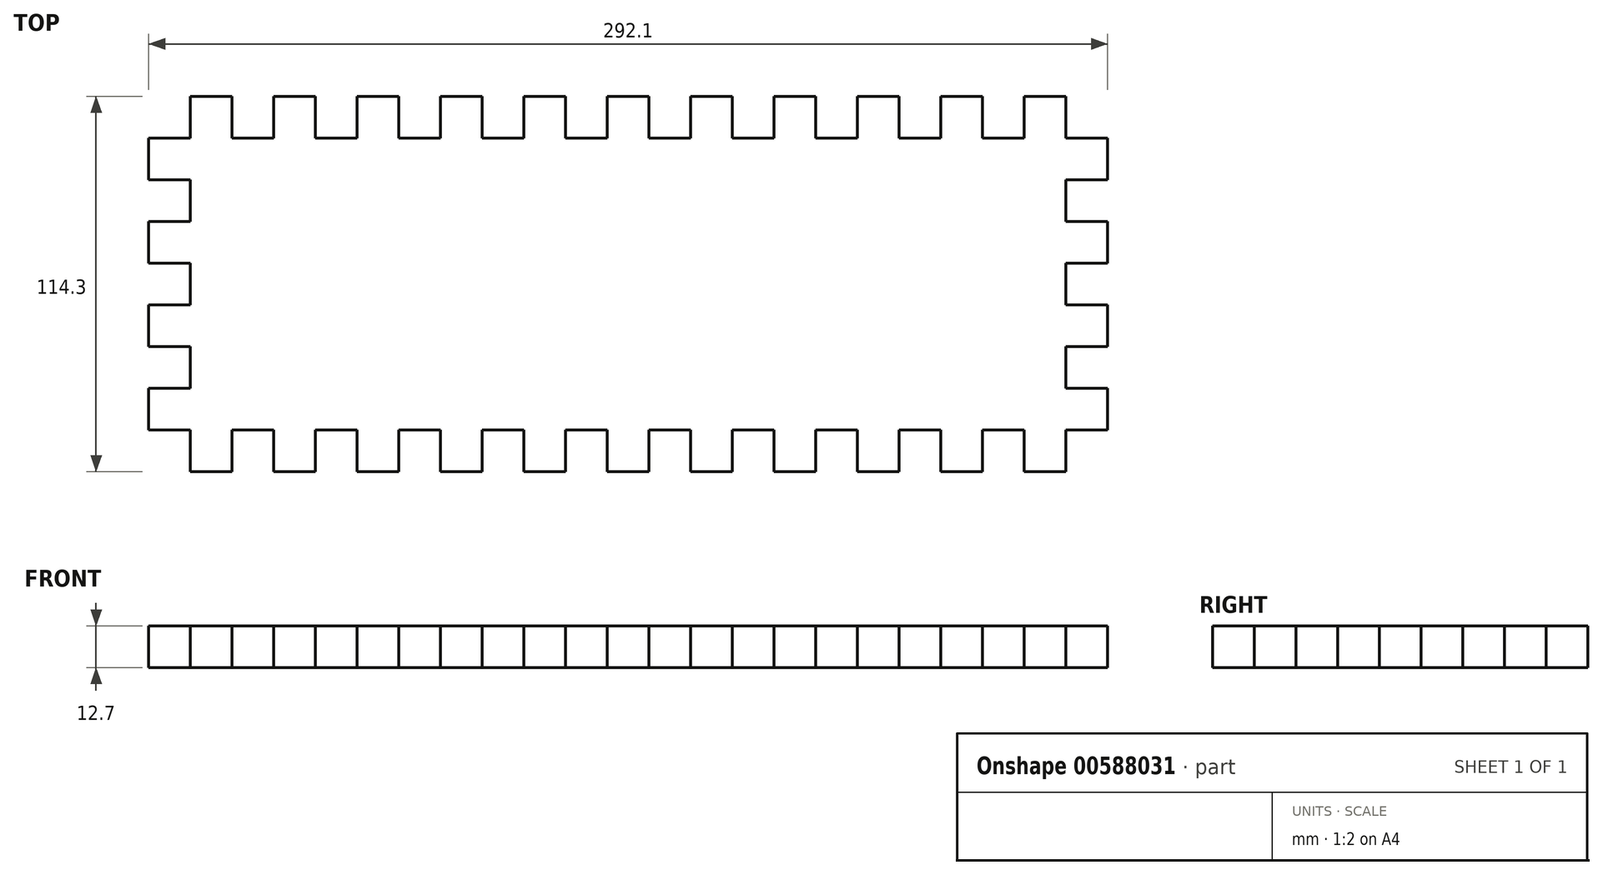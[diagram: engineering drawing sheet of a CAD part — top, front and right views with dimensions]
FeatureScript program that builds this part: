
annotation { "Feature Type Name" : "Feature", "Feature Type Description" : "" }
export const myFeature = defineFeature(function(context is Context, id is Id, definition is map)
    precondition{}
    {
        {
            var Q0;
            Q0=qCreatedBy(makeId("Top.planeOp"),FACE);
            var sketch = newSketch(context, id + "F0", { "sketchPlane" : qUnion([Q0])});
            skLineSegment(sketch, "E0.top", {"start": v(12.7, 114.3) * mm, "end": v(25.4, 114.3) * mm});
            skLineSegment(sketch, "E0.right", {"start": v(292.1, 12.7) * mm, "end": v(292.1, 25.4) * mm});
            skLineSegment(sketch, "E1", {"start": v(25.4, 101.6) * mm, "end": v(38.1, 101.6) * mm});
            skLineSegment(sketch, "E2", {"start": v(279.4, 88.9) * mm, "end": v(279.4, 76.2) * mm});
            skLineSegment(sketch, "E3", {"start": v(12.7, 101.6) * mm, "end": v(12.7, 114.3) * mm});
            skLineSegment(sketch, "E4", {"start": v(12.7, 101.6) * mm, "end": v(0, 101.6) * mm});
            skLineSegment(sketch, "E5.1.0.0", {"start": v(25.4, 101.6) * mm, "end": v(25.4, 114.3) * mm});
            skLineSegment(sketch, "E5.2.0.0", {"start": v(38.1, 101.6) * mm, "end": v(38.1, 114.3) * mm});
            skLineSegment(sketch, "E5.3.0.0", {"start": v(50.8, 101.6) * mm, "end": v(50.8, 114.3) * mm});
            skLineSegment(sketch, "E5.4.0.0", {"start": v(63.5, 101.6) * mm, "end": v(63.5, 114.3) * mm});
            skLineSegment(sketch, "E5.5.0.0", {"start": v(76.2, 101.6) * mm, "end": v(76.2, 114.3) * mm});
            skLineSegment(sketch, "E5.6.0.0", {"start": v(88.9, 101.6) * mm, "end": v(88.9, 114.3) * mm});
            skLineSegment(sketch, "E5.7.0.0", {"start": v(101.6, 101.6) * mm, "end": v(101.6, 114.3) * mm});
            skLineSegment(sketch, "E5.8.0.0", {"start": v(114.3, 101.6) * mm, "end": v(114.3, 114.3) * mm});
            skLineSegment(sketch, "E5.9.0.0", {"start": v(127, 101.6) * mm, "end": v(127, 114.3) * mm});
            skLineSegment(sketch, "E5.10.0.0", {"start": v(139.7, 101.6) * mm, "end": v(139.7, 114.3) * mm});
            skLineSegment(sketch, "E5.11.0.0", {"start": v(152.4, 101.6) * mm, "end": v(152.4, 114.3) * mm});
            skLineSegment(sketch, "E5.12.0.0", {"start": v(165.1, 101.6) * mm, "end": v(165.1, 114.3) * mm});
            skLineSegment(sketch, "E5.13.0.0", {"start": v(177.8, 101.6) * mm, "end": v(177.8, 114.3) * mm});
            skLineSegment(sketch, "E5.14.0.0", {"start": v(190.5, 101.6) * mm, "end": v(190.5, 114.3) * mm});
            skLineSegment(sketch, "E5.15.0.0", {"start": v(203.2, 101.6) * mm, "end": v(203.2, 114.3) * mm});
            skLineSegment(sketch, "E5.16.0.0", {"start": v(215.9, 101.6) * mm, "end": v(215.9, 114.3) * mm});
            skLineSegment(sketch, "E5.17.0.0", {"start": v(228.6, 101.6) * mm, "end": v(228.6, 114.3) * mm});
            skLineSegment(sketch, "E5.18.0.0", {"start": v(241.3, 101.6) * mm, "end": v(241.3, 114.3) * mm});
            skLineSegment(sketch, "E5.19.0.0", {"start": v(254, 101.6) * mm, "end": v(254, 114.3) * mm});
            skLineSegment(sketch, "E5.20.0.0", {"start": v(266.7, 101.6) * mm, "end": v(266.7, 114.3) * mm});
            skLineSegment(sketch, "E5.21.0.0", {"start": v(279.4, 101.6) * mm, "end": v(279.4, 114.3) * mm});
            skLineSegment(sketch, "E6.trimOffspring", {"start": v(38.1, 114.3) * mm, "end": v(50.8, 114.3) * mm});
            skLineSegment(sketch, "E7.trimOffspring", {"start": v(63.5, 114.3) * mm, "end": v(76.2, 114.3) * mm});
            skLineSegment(sketch, "E8.trimOffspring", {"start": v(88.9, 114.3) * mm, "end": v(101.6, 114.3) * mm});
            skLineSegment(sketch, "E9.trimOffspring", {"start": v(114.3, 114.3) * mm, "end": v(127, 114.3) * mm});
            skLineSegment(sketch, "E10.trimOffspring", {"start": v(139.7, 114.3) * mm, "end": v(152.4, 114.3) * mm});
            skLineSegment(sketch, "E11.trimOffspring", {"start": v(165.1, 114.3) * mm, "end": v(177.8, 114.3) * mm});
            skLineSegment(sketch, "E12.trimOffspring", {"start": v(190.5, 114.3) * mm, "end": v(203.2, 114.3) * mm});
            skLineSegment(sketch, "E13.trimOffspring", {"start": v(215.9, 114.3) * mm, "end": v(228.6, 114.3) * mm});
            skLineSegment(sketch, "E14.trimOffspring", {"start": v(241.3, 114.3) * mm, "end": v(254, 114.3) * mm});
            skLineSegment(sketch, "E15.trimOffspring", {"start": v(266.7, 114.3) * mm, "end": v(279.4, 114.3) * mm});
            skLineSegment(sketch, "E16.trimOffspring", {"start": v(254, 101.6) * mm, "end": v(266.7, 101.6) * mm});
            skLineSegment(sketch, "E17.trimOffspring", {"start": v(228.6, 101.6) * mm, "end": v(241.3, 101.6) * mm});
            skLineSegment(sketch, "E18.trimOffspring", {"start": v(203.2, 101.6) * mm, "end": v(215.9, 101.6) * mm});
            skLineSegment(sketch, "E19.trimOffspring", {"start": v(177.8, 101.6) * mm, "end": v(190.5, 101.6) * mm});
            skLineSegment(sketch, "E20.trimOffspring", {"start": v(152.4, 101.6) * mm, "end": v(165.1, 101.6) * mm});
            skLineSegment(sketch, "E21.trimOffspring", {"start": v(127, 101.6) * mm, "end": v(139.7, 101.6) * mm});
            skLineSegment(sketch, "E22.trimOffspring", {"start": v(101.6, 101.6) * mm, "end": v(114.3, 101.6) * mm});
            skLineSegment(sketch, "E23.trimOffspring", {"start": v(76.2, 101.6) * mm, "end": v(88.9, 101.6) * mm});
            skLineSegment(sketch, "E24.trimOffspring", {"start": v(50.8, 101.6) * mm, "end": v(63.5, 101.6) * mm});
            skLineSegment(sketch, "E25", {"start": v(279.4, 101.6) * mm, "end": v(292.1, 101.6) * mm});
            skLineSegment(sketch, "E26.0.1.0", {"start": v(279.4, 88.9) * mm, "end": v(292.1, 88.9) * mm});
            skLineSegment(sketch, "E26.0.2.0", {"start": v(279.4, 76.2) * mm, "end": v(292.1, 76.2) * mm});
            skLineSegment(sketch, "E26.0.3.0", {"start": v(279.4, 63.5) * mm, "end": v(292.1, 63.5) * mm});
            skLineSegment(sketch, "E26.0.4.0", {"start": v(279.4, 50.8) * mm, "end": v(292.1, 50.8) * mm});
            skLineSegment(sketch, "E26.0.5.0", {"start": v(279.4, 38.1) * mm, "end": v(292.1, 38.1) * mm});
            skLineSegment(sketch, "E26.0.6.0", {"start": v(279.4, 25.4) * mm, "end": v(292.1, 25.4) * mm});
            skLineSegment(sketch, "E26.0.7.0", {"start": v(279.4, 12.7) * mm, "end": v(292.1, 12.7) * mm});
            skLineSegment(sketch, "E27.trimOffspring", {"start": v(279.4, 63.5) * mm, "end": v(279.4, 50.8) * mm});
            skLineSegment(sketch, "E28.trimOffspring", {"start": v(279.4, 38.1) * mm, "end": v(279.4, 25.4) * mm});
            skLineSegment(sketch, "E29.trimOffspring", {"start": v(292.1, 38.1) * mm, "end": v(292.1, 50.8) * mm});
            skLineSegment(sketch, "E30.trimOffspring", {"start": v(292.1, 63.5) * mm, "end": v(292.1, 76.2) * mm});
            skLineSegment(sketch, "E31.trimOffspring", {"start": v(292.1, 88.9) * mm, "end": v(292.1, 101.6) * mm});
            skLineSegment(sketch, "E32", {"start": v(279.4, 12.7) * mm, "end": v(279.4, 0) * mm});
            skLineSegment(sketch, "E33.MirrorCS", {"start": v(0, 63.5) * mm, "end": v(0, 76.2) * mm});
            skLineSegment(sketch, "E34.MirrorCS", {"start": v(12.7, 38.1) * mm, "end": v(12.7, 25.4) * mm});
            skLineSegment(sketch, "E35.MirrorCS", {"start": v(12.7, 12.7) * mm, "end": v(0, 12.7) * mm});
            skLineSegment(sketch, "E36.MirrorCS", {"start": v(12.7, 76.2) * mm, "end": v(0, 76.2) * mm});
            skLineSegment(sketch, "E37.MirrorCS", {"start": v(12.7, 25.4) * mm, "end": v(0, 25.4) * mm});
            skLineSegment(sketch, "E38.MirrorCS", {"start": v(12.7, 38.1) * mm, "end": v(0, 38.1) * mm});
            skLineSegment(sketch, "E39.MirrorCS", {"start": v(12.7, 88.9) * mm, "end": v(0, 88.9) * mm});
            skLineSegment(sketch, "E40.MirrorCS", {"start": v(12.7, 12.7) * mm, "end": v(12.7, 0) * mm});
            skLineSegment(sketch, "E41.MirrorCS", {"start": v(12.7, 50.8) * mm, "end": v(0, 50.8) * mm});
            skLineSegment(sketch, "E42.MirrorCS", {"start": v(12.7, 63.5) * mm, "end": v(12.7, 50.8) * mm});
            skLineSegment(sketch, "E43.MirrorCS", {"start": v(0, 38.1) * mm, "end": v(0, 50.8) * mm});
            skLineSegment(sketch, "E44.MirrorCS", {"start": v(0, 12.7) * mm, "end": v(0, 25.4) * mm});
            skLineSegment(sketch, "E45.MirrorCS", {"start": v(12.7, 88.9) * mm, "end": v(12.7, 76.2) * mm});
            skLineSegment(sketch, "E46.MirrorCS", {"start": v(0, 88.9) * mm, "end": v(0, 101.6) * mm});
            skLineSegment(sketch, "E47.MirrorCS", {"start": v(12.7, 63.5) * mm, "end": v(0, 63.5) * mm});
            skLineSegment(sketch, "E48.MirrorCS", {"start": v(139.7, 0) * mm, "end": v(152.4, 0) * mm});
            skLineSegment(sketch, "E49.MirrorCS", {"start": v(63.5, 0) * mm, "end": v(76.2, 0) * mm});
            skLineSegment(sketch, "E50.MirrorCS", {"start": v(76.2, 12.7) * mm, "end": v(88.9, 12.7) * mm});
            skLineSegment(sketch, "E51.MirrorCS", {"start": v(152.4, 12.7) * mm, "end": v(165.1, 12.7) * mm});
            skLineSegment(sketch, "E52.MirrorCS", {"start": v(266.7, 12.7) * mm, "end": v(266.7, 0) * mm});
            skLineSegment(sketch, "E53.MirrorCS", {"start": v(177.8, 12.7) * mm, "end": v(177.8, 0) * mm});
            skLineSegment(sketch, "E54.MirrorCS", {"start": v(215.9, 0) * mm, "end": v(228.6, 0) * mm});
            skLineSegment(sketch, "E55.MirrorCS", {"start": v(165.1, 0) * mm, "end": v(177.8, 0) * mm});
            skLineSegment(sketch, "E56.MirrorCS", {"start": v(241.3, 12.7) * mm, "end": v(241.3, 0) * mm});
            skLineSegment(sketch, "E57.MirrorCS", {"start": v(177.8, 12.7) * mm, "end": v(190.5, 12.7) * mm});
            skLineSegment(sketch, "E58.MirrorCS", {"start": v(152.4, 12.7) * mm, "end": v(152.4, 0) * mm});
            skLineSegment(sketch, "E59.MirrorCS", {"start": v(241.3, 0) * mm, "end": v(254, 0) * mm});
            skLineSegment(sketch, "E60.MirrorCS", {"start": v(38.1, 0) * mm, "end": v(50.8, 0) * mm});
            skLineSegment(sketch, "E61.MirrorCS", {"start": v(127, 12.7) * mm, "end": v(139.7, 12.7) * mm});
            skLineSegment(sketch, "E62.MirrorCS", {"start": v(254, 12.7) * mm, "end": v(254, 0) * mm});
            skLineSegment(sketch, "E63.MirrorCS", {"start": v(203.2, 12.7) * mm, "end": v(215.9, 12.7) * mm});
            skLineSegment(sketch, "E64.MirrorCS", {"start": v(165.1, 12.7) * mm, "end": v(165.1, 0) * mm});
            skLineSegment(sketch, "E65.MirrorCS", {"start": v(139.7, 12.7) * mm, "end": v(139.7, 0) * mm});
            skLineSegment(sketch, "E66.MirrorCS", {"start": v(228.6, 12.7) * mm, "end": v(228.6, 0) * mm});
            skLineSegment(sketch, "E67.MirrorCS", {"start": v(228.6, 12.7) * mm, "end": v(241.3, 12.7) * mm});
            skLineSegment(sketch, "E68.MirrorCS", {"start": v(25.4, 12.7) * mm, "end": v(38.1, 12.7) * mm});
            skLineSegment(sketch, "E69.MirrorCS", {"start": v(12.7, 0) * mm, "end": v(25.4, 0) * mm});
            skLineSegment(sketch, "E70.MirrorCS", {"start": v(114.3, 12.7) * mm, "end": v(114.3, 0) * mm});
            skLineSegment(sketch, "E71.MirrorCS", {"start": v(25.4, 12.7) * mm, "end": v(25.4, 0) * mm});
            skLineSegment(sketch, "E72.MirrorCS", {"start": v(38.1, 12.7) * mm, "end": v(38.1, 0) * mm});
            skLineSegment(sketch, "E73.MirrorCS", {"start": v(50.8, 12.7) * mm, "end": v(50.8, 0) * mm});
            skLineSegment(sketch, "E74.MirrorCS", {"start": v(127, 12.7) * mm, "end": v(127, 0) * mm});
            skLineSegment(sketch, "E75.MirrorCS", {"start": v(190.5, 0) * mm, "end": v(203.2, 0) * mm});
            skLineSegment(sketch, "E76.MirrorCS", {"start": v(190.5, 12.7) * mm, "end": v(190.5, 0) * mm});
            skLineSegment(sketch, "E77.MirrorCS", {"start": v(63.5, 12.7) * mm, "end": v(63.5, 0) * mm});
            skLineSegment(sketch, "E78.MirrorCS", {"start": v(76.2, 12.7) * mm, "end": v(76.2, 0) * mm});
            skLineSegment(sketch, "E79.MirrorCS", {"start": v(114.3, 0) * mm, "end": v(127, 0) * mm});
            skLineSegment(sketch, "E80.MirrorCS", {"start": v(215.9, 12.7) * mm, "end": v(215.9, 0) * mm});
            skLineSegment(sketch, "E81.MirrorCS", {"start": v(203.2, 12.7) * mm, "end": v(203.2, 0) * mm});
            skLineSegment(sketch, "E82.MirrorCS", {"start": v(101.6, 12.7) * mm, "end": v(114.3, 12.7) * mm});
            skLineSegment(sketch, "E83.MirrorCS", {"start": v(266.7, 0) * mm, "end": v(279.4, 0) * mm});
            skLineSegment(sketch, "E84.MirrorCS", {"start": v(50.8, 12.7) * mm, "end": v(63.5, 12.7) * mm});
            skLineSegment(sketch, "E85.MirrorCS", {"start": v(254, 12.7) * mm, "end": v(266.7, 12.7) * mm});
            skLineSegment(sketch, "E86.MirrorCS", {"start": v(88.9, 0) * mm, "end": v(101.6, 0) * mm});
            skLineSegment(sketch, "E87.MirrorCS", {"start": v(88.9, 12.7) * mm, "end": v(88.9, 0) * mm});
            skLineSegment(sketch, "E88.MirrorCS", {"start": v(101.6, 12.7) * mm, "end": v(101.6, 0) * mm});
            skSolve(sketch);
        }
        {
            var Q0;
            Q0 = qSketchRegion(id + "F0", true);
            extrude(context, id + "F1", {"entities" : qUnion([Q0]), "depth" : 12.7 * mm, "offsetDistance" : 25.4 * mm});
        }
    });
